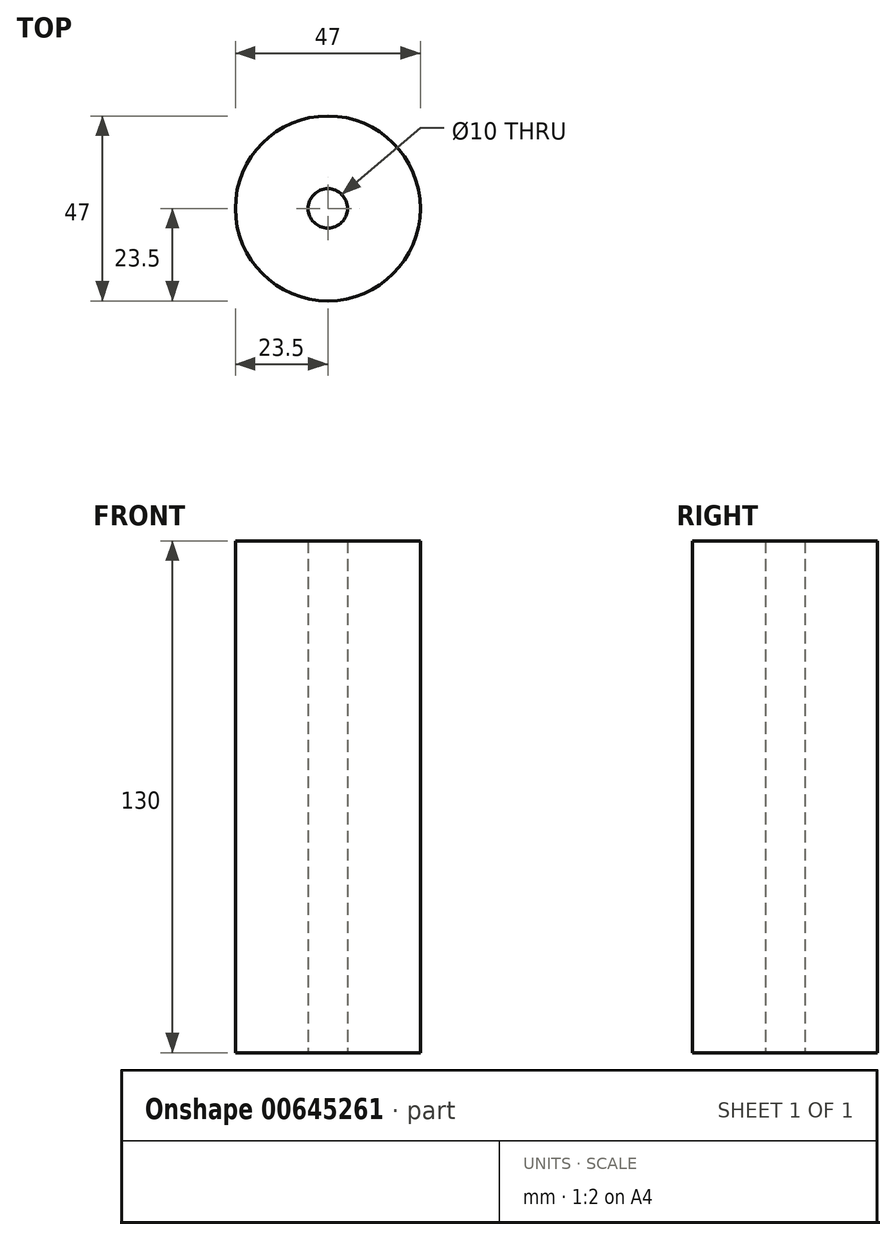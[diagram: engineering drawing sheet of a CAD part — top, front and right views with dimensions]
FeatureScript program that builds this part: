
annotation { "Feature Type Name" : "Feature", "Feature Type Description" : "" }
export const myFeature = defineFeature(function(context is Context, id is Id, definition is map)
    precondition{}
    {
        {
            var Q0;
            Q0=qCreatedBy(makeId("Top.planeOp"),FACE);
            var sketch = newSketch(context, id + "F0", { "sketchPlane" : qUnion([Q0])});
            skCircle(sketch, "E0", {"center": v(0, 0) * mm, "radius": 5 * mm});
            skCircle(sketch, "E1", {"center": v(0, 0) * mm, "radius": 23.5 * mm});
            skSolve(sketch);
        }
        {
            var Q0;
            Q0 = qSketchRegion(id + "F0", true);
            extrude(context, id + "F1", {"entities" : qUnion([Q0]), "depth" : 130 * mm, "offsetDistance" : 25 * mm});
        }
    });
